# Revit family: 0049104 Feilo Sylvania Lighting Fixture SYLVEO LED 3000LM WIDE 3K
name_source: partatom
category: Lighting Fixtures
revit_build: Autodesk Revit 2017 (Build: 20190507_1515(x64)
units: mm (PartAtom-declared; Revit-internal decimal feet)

## family parameters
Cut with Voids When Loaded = No
Host = Face
Light Source = No
OmniClass Number = 23.80.70.00
OmniClass Title = Lighting
Part Type = Normal
Room Calculation Point = No
Round Connector Dimension = Use Diameter
Shared = No

## types (1)
- 0049104 SYLVEO LED 3000LM WIDE 3K
    Apparent Load = 31 VA
    Assembly Code = D5020200
    AssetType = Fixed
    BracketExtrusionEnd = 13 mm
    BracketExtrusionStart = -13 mm  [stored -0.0426509 ft]
    BracketInnerWidth = 183 mm
    BracketWidth = 25 mm  [stored 0.082021 ft]
    ClassificationName = Uniclass2015
    ClassificationValue = EF_70_80
    Color = Aluminium
    ColorConsistency(SDCM) = 6
    ColorTemperature = 4000 K
    Cost = 0 $
    Default Elevation = 1219 mm
    Description = Exterior LED Floodlight, comes complete with a 1000mm cable and adjustable bracket, aluminium housing, clear glass diffuser, IP66, IK08, Class I, 3000K, Non-dimming, 3090lm, 31W, 101lm/W, 850mA, CRI70, 52° beam angle, 50000hrs, (LxWxD) 49x205x219mm
    Diffuser Finish = Clear
    Diffuser Material = Glass
    DimmingControlOptions = Non dimmable
    DocumentationLiterature = http://www.sylvania-lighting.com
    DurationUnit = hours
    ElectricShockClassification = Class I
    ExpectedLife = 50000
    Finish = Die cast
    IfcExportAs = IfcLightFixtureType
    IfcExportType = IfcLightFixtureType
    ImpactProtectionIndex = IK08
    IngressProtection = IP66
    InputNominalFrequency = 50 Hz
    InputVoltage = 100-240V~
    Keynote = 16500
    Lamp = LED
    LampsColourRenderingIndex = 70
    LampsType = LED
    LightOutputRatio = 100
    LuminousFlux = 3189 lm
    Manufacturer = Feilo Sylvania
    ManufacturerName = Feilo Sylvania
    Material = aluminium housing, glass diffuser
    Material_1_FEILO = <By Category>
    Material_2_FEILO = Default
    Material_3_FEILO = Diffuser-Sylvania-Glow
    Material_4_FEILO = <By Category>
    Model = SYLVEO LED 3000LM WIDE 3K
    ModelNumber = 0049104
    ModelReference = SYLVEO LED 3000LM WIDE 3K
    Name = SYLVEO LED 3000LM WIDE 3K
    NominalDepth = 59 mm
    NominalHeight = 219 mm  [stored 0.718504 ft]
    NominalLength = 205 mm
    PhotobiologicalRiskGroup = RG1
    PowerConsumption = 30.5 W
    PowerFactor = 0
    TotalWidth = 205 mm
    Type Image = <None>
    TypeBody_FEILO = Sylveo Body S : 0049104 SYLVEO LED 3000LM WIDE 3K
    TypeName = SYLVEO LED 3000LM WIDE 3K
    URL = http://www.sylvania-lighting.com
    Voltage = 230 V
    Weight = 11.028 kg
    _BimSpecGuid = 0
    _BimstoreBibleVersion = Version 15
    _CurrentRevision = 0

note: [stored X ft] marks values corroborated as IEEE doubles in the binary element streams (Revit-internal decimal feet)

## geometry (parser evidence)
native form markers: Extrusion x2, Sweep x5
no freeform markers — native parametric forms only
